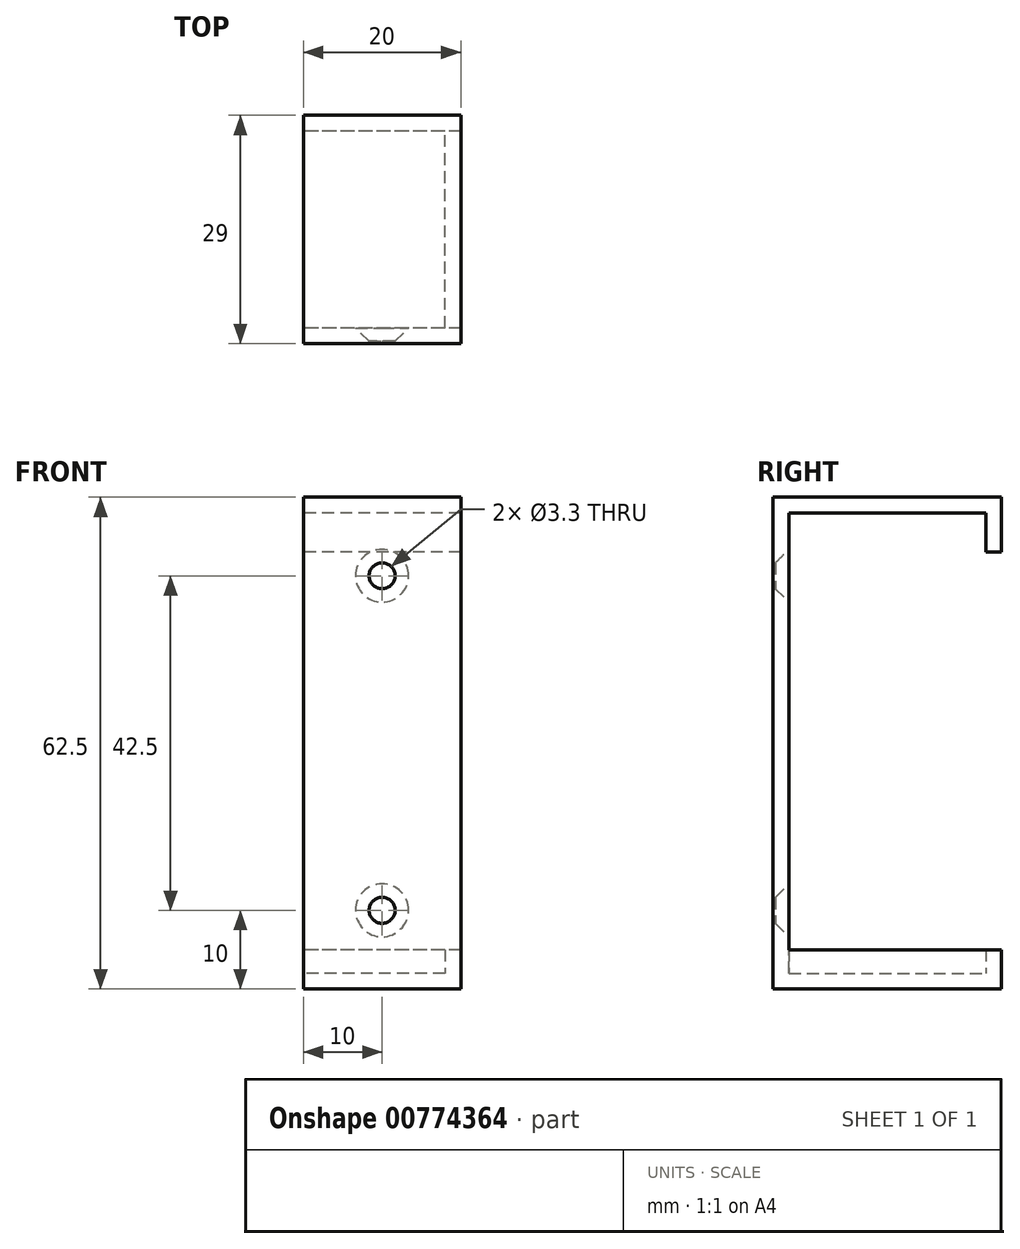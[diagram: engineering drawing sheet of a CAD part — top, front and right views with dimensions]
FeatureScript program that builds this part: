
annotation { "Feature Type Name" : "Feature", "Feature Type Description" : "" }
export const myFeature = defineFeature(function(context is Context, id is Id, definition is map)
    precondition{}
    {
        {
            var Q0;
            Q0=qCreatedBy(makeId("Right.planeOp"),FACE);
            var sketch = newSketch(context, id + "F0", { "sketchPlane" : qUnion([Q0])});
            skLineSegment(sketch, "E0.bottom", {"start": v(14.5, -31.25) * mm, "end": v(-14.5, -31.25) * mm});
            skLineSegment(sketch, "E0.top", {"start": v(14.5, 31.25) * mm, "end": v(-14.5, 31.25) * mm});
            skLineSegment(sketch, "E0.left", {"start": v(14.5, -31.25) * mm, "end": v(14.5, 31.25) * mm});
            skLineSegment(sketch, "E0.right", {"start": v(-14.5, -31.25) * mm, "end": v(-14.5, 31.25) * mm});
            skPoint(sketch, "E0.middle", {"position": v(0, 0) * mm});
            skLineSegment(sketch, "E1.0", {"start": v(12.5, 29.25) * mm, "end": v(-12.5, 29.25) * mm});
            skLineSegment(sketch, "E1.1", {"start": v(12.5, -29.25) * mm, "end": v(12.5, 29.25) * mm});
            skLineSegment(sketch, "E1.2", {"start": v(12.5, -29.25) * mm, "end": v(-12.5, -29.25) * mm});
            skLineSegment(sketch, "E1.3", {"start": v(-12.5, -29.25) * mm, "end": v(-12.5, 29.25) * mm});
            skSolve(sketch);
        }
        {
            var Q0;
            Q0=makeQuery(id+"F0.imprint","IMPRINT",FACE,{"disambiguationData":[TD([[makeQuery(id+"F0.imprint","IMPRINT",EDGE,{"derivedFrom":sQuery(id+"F0.wireOp",EDGE,"E0.bottom")}),-1.0]])]});
            extrude(context, id + "F1", {"entities" : qUnion([Q0]), "depth" : 20 * mm, "offsetDistance" : 25 * mm});
        }
        {
            var Q0;
            Q0=makeQuery(id+"F1.opExtrude","SWEPT_FACE",FACE,{"disambiguationData":[OSD([sQuery(id+"F0.wireOp",EDGE,"E0.left")])]});
            var sketch = newSketch(context, id + "F2", { "sketchPlane" : qUnion([Q0])});
            skLineSegment(sketch, "E2.bottom", {"start": v(-20, 26.25) * mm, "end": v(0, 26.25) * mm});
            skLineSegment(sketch, "E2.top", {"start": v(-20, -26.25) * mm, "end": v(0, -26.25) * mm});
            skLineSegment(sketch, "E2.left", {"start": v(-20, 26.25) * mm, "end": v(-20, -26.25) * mm});
            skLineSegment(sketch, "E2.right", {"start": v(0, 26.25) * mm, "end": v(0, -26.25) * mm});
            skSolve(sketch);
        }
        {
            var Q0;
            Q0=makeQuery(id+"F2.imprint","IMPRINT",FACE,{"disambiguationData":[TD([[makeQuery(id+"F2.imprint","IMPRINT",EDGE,{"derivedFrom":sQuery(id+"F2.wireOp",EDGE,"E2.bottom")}),-1.0]])]});
            extrude(context, id + "F3", {"entities" : qUnion([Q0]), "operationType" : NewBodyOperationType.REMOVE, "oppositeDirection" : true, "depth" : 2 * mm, "offsetDistance" : 25 * mm});
        }
        {
            var Q0;
            Q0=makeQuery(id+"F1.opExtrude","SWEPT_FACE",FACE,{"disambiguationData":[OSD([sQuery(id+"F0.wireOp",EDGE,"E1.3")])]});
            var sketch = newSketch(context, id + "F4", { "sketchPlane" : qUnion([Q0])});
            skLineSegment(sketch, "E3", {"start": v(-10, 28.15) * mm, "end": v(-10, -27.84) * mm, "construction": true});
            skPoint(sketch, "E3.startSnap0", {"position": v(-10, 29.25) * mm});
            skPoint(sketch, "E4", {"position": v(-10, 21.25) * mm});
            skPoint(sketch, "E5", {"position": v(-10, -21.25) * mm});
            skSolve(sketch);
        }
        {
            var Q0;
            Q0=sQuery(id+"F4.wireOp",VERTEX,"E4");
            var Q1;
            Q1=sQuery(id+"F4.wireOp",VERTEX,"E5");
            var Q2;
            Q2=makeQuery(id+"F1.opExtrude","SWEPT_BODY",BODY,{"disambiguationData":[OSD([sQuery(id+"F0.wireOp",EDGE,"E0.bottom"),sQuery(id+"F0.wireOp",EDGE,"E0.top"),sQuery(id+"F0.wireOp",EDGE,"E0.left"),sQuery(id+"F0.wireOp",EDGE,"E0.right"),sQuery(id+"F0.wireOp",EDGE,"E1.0"),sQuery(id+"F0.wireOp",EDGE,"E1.1"),sQuery(id+"F0.wireOp",EDGE,"E1.2"),sQuery(id+"F0.wireOp",EDGE,"E1.3")])]});
            hole(context, id + "F5", {"style" : HoleStyle.C_SINK, "endStyle" : HoleEndStyle.THROUGH, "standardTappedOrClearance" : lookupTablePath({ "standard" : "ISO", "fit" : "Normal", "size" : "M3", "type" : "Clearance" }), "standardBlindInLast" : lookupTablePath({ "fit" : "Standard", "standard" : "ISO", "size" : "M3", "type" : "Clearance" }), "holeDiameter" : 3.3 * mm, "cSinkDiameter" : 6.72 * mm, "cSinkAngle" : 90 * degree, "majorDiameter" : 5 * mm, "isTappedThrough" : true, "tappedDepth" : 12 * mm, "tapClearance" : 3, "locations" : qUnion([Q0, Q1]), "scope" : qUnion([Q2])});
        }
        {
            var Q0;
            Q0=makeQuery(id+"F1.opExtrude","SWEPT_FACE",FACE,{"disambiguationData":[OSD([sQuery(id+"F0.wireOp",EDGE,"E1.2")])]});
            var sketch = newSketch(context, id + "F6", { "sketchPlane" : qUnion([Q0])});
            skLineSegment(sketch, "E6", {"start": v(18, -12.5) * mm, "end": v(18, 12.5) * mm});
            skSolve(sketch);
        }
        {
            var Q0;
            {var subQ0=sQuery(id+"F6.wireOp",EDGE,"E6");Q0=makeQuery(id+"F6.imprint","IMPRINT",FACE,{"disambiguationData":[TD([[makeQuery(id+"F6.imprint","IMPRINT",EDGE,{"derivedFrom":subQ0}),-1.0]])]});}
            var Q1;
            Q1=makeQuery(id+"F3.boolean.opBoolean","COPY",VERTEX,{"derivedFrom":makeQuery(id+"F3.opExtrude","CAP_VERTEX",VERTEX,{"disambiguationData":[OSD([sQuery(id+"F0.wireOp",EDGE,"E0.left"),sQuery(id+"F2.wireOp",EDGE,"E2.top"),sQuery(id+"F2.wireOp",EDGE,"E2.left")])],"isStart":false})});
            extrude(context, id + "F7", {"entities" : qUnion([Q0]), "operationType" : NewBodyOperationType.ADD, "endBound" : BoundingType.UP_TO_VERTEX, "depth" : 25 * mm, "endBoundEntityVertex" : qUnion([Q1]), "offsetDistance" : 25 * mm});
        }
        {
            var Q0;
            Q0=makeQuery(id+"F3.boolean.opBoolean","COPY",FACE,{"derivedFrom":makeQuery(id+"F3.opExtrude","SWEPT_FACE",FACE,{"disambiguationData":[OSD([sQuery(id+"F2.wireOp",EDGE,"E2.bottom")])]})});
            extrude(context, id + "F8", {"entities" : qUnion([Q0]), "operationType" : NewBodyOperationType.ADD, "depth" : 2 * mm, "offsetDistance" : 25 * mm});
        }
    });
